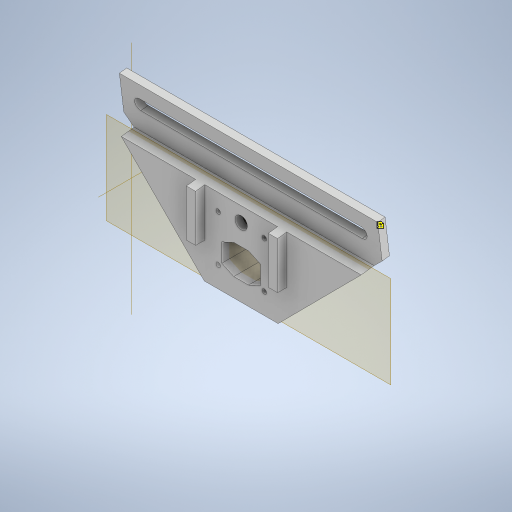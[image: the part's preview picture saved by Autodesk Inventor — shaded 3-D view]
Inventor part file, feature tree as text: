
AUTODESK INVENTOR PART (.ipt)
format: ipt  version: 2023 (Build 270158000, 158)  size: 479,232 bytes
history: native  units: mm
features: extrude x15, sketch x15, plane x7
ambient origin geometry x8: Origin, YZ Plane, XZ Plane, XY Plane, X Axis, Y Axis, Z Axis, Center Point
bodies: Volumenkörper1 (feature_tree)
feature tree (37):
  extrude  "Extrusion1"  Depth=105.0mm
  plane  "Arbeitsebene1"
  plane  "Arbeitsebene2"
  extrude  "Extrusion6"  Depth=140.0mm TaperAngle=0.0deg
  extrude  "Extrusion7"  [1 undecoded]
  plane  "Arbeitsebene3"
  plane  "Arbeitsebene4"
  plane  "Arbeitsebene5"
  extrude  "Extrusion14"  Depth=25.0mm
  extrude  "Extrusion15"  Depth=10.0mm
  extrude  "Extrusion16"  Depth=10.0mm
  extrude  "Extrusion17"  Depth=10.0mm TaperAngle=0.0deg
  plane  "Arbeitsebene6"
  extrude  "Extrusion18"  Depth=7.0mm
  extrude  "Extrusion19"  Depth=10.0mm
  extrude  "Extrusion20"  [1 undecoded]
  extrude  "Extrusion21"  Depth=10.0mm TaperAngle=0.0deg
  plane  "Arbeitsebene7"
  extrude  "Extrusion22"  Depth=45.0mm
  extrude  "Extrusion23"  Depth=2.5mm
  extrude  "Extrusion24"  Depth=2.5mm
  extrude  "Extrusion25"  Depth=10.0mm
  sketch  "Skizze1"  dims[d0=16.929694mm d1=105.0mm]
  sketch  "Skizze6"  dims[d2=8.0mm d3=140.0mm d4=0.0mm]
  sketch  "Skizze7"  dims[d10=-4.0mm d18=-4.0mm]
  sketch  "Skizze18"  dims[d21=0.0mm d22=0.0mm d23=25.0mm]
  sketch  "Skizze19"  dims[d24=25.0mm d25=10.0mm]
  sketch  "Skizze20"  dims[d26=10.0mm d27=6.0mm]
  sketch  "Skizze21"  dims[d28=7.0mm d29=10.0mm d30=0.0mm]
  sketch  "Skizze23"  dims[d31=6.0mm d32=7.0mm]
  sketch  "Skizze24"  dims[d33=10.0mm d34=10.0mm]
  sketch  "Skizze27"  dims[d65=-4.0mm d74=-70.0mm]
  sketch  "Skizze28"  dims[d84=2.0mm d85=10.0mm d86=0.0mm]
  sketch  "Skizze29"  dims[d87=10.0mm d88=0.0mm d89=45.0mm]
  sketch  "Skizze31"  dims[d90=0.0mm d91=0.0mm d92=2.5mm]
  sketch  "Skizze33"  dims[d93=2.5mm d94=2.5mm]
  sketch  "Skizze34"  dims[d95=2.5mm d96=25.0mm d97=25.0mm d98=25.0mm d100=12.5mm d101=9.0mm d102=9.322797mm d103=0.0mm d104=0.0mm d105=-4.0mm d106=5.0mm d107=5.0mm d108=5.0mm d109=5.0mm d110=0.0mm d111=0.0mm d112=8.0mm d113=16.0mm d114=10.0mm d116=21.0mm d118=10.0mm d119=0.0mm d120=6.7mm d121=8.0mm d122=0.0mm d123=0.0mm d124=19.7mm d125=19.7mm d126=5.0mm d127=5.0mm d128=18.0mm d129=18.0mm d130=5.0mm d131=0.0mm d132=0.0mm d133=0.0mm d134=10.5mm d135=10.0mm d136=0.0mm d137=10.0mm d138=0.0mm d139=50.0mm d140=50.0mm d141=50.0mm d142=50.0mm d143=0.0mm d144=0.0mm]
note: 2 required parameter values undecoded (feature->parameter linkage not recoverable at this tier; creation-order binding heuristic only, values carry confidence <= 0.55)
